# Revit family: IS_LDV_E2639_BIM_GB
name_source: partatom
category: Plumbing Fixtures
units: mm (PartAtom-declared; Revit-internal decimal feet)

## family parameters
Cut with Voids When Loaded = No
Host = Face
Maintain Annotation Orientation = No
OmniClass Number = 23.45.05.14.14.14
OmniClass Title = Clinic Sinks
Part Type = Normal
Room Calculation Point = No
Round Connector Dimension = Use Diameter
Shared = Yes

## types (1)
- E263901 - LDV BTW HF BIDET WHITE BXD
    Accessories = https://www.idealstandard.co.uk
    AreaUnits = millimeters
    Assembly Code = C1030200
    AssetType = Fixed
    BIMObjectName = IS_LDV_Bidet_E2639
    BarCode = 5017830562481
    Brand = Ideal Standard
    CWFU = 0
    Color = White
    ConnectionType = Plumbing
    Cost = 0 $
    Default Elevation = 400 mm  [stored 1.31234 ft]
    Description = La Dolce Vita® back-to-wall bidet, hidden wallfixation TT0293851, 1 taphole, with round overflow, white
    DrainSize = 46 mm  [stored 0.150919 ft]
    DurationUnit = year
    ECA = No
    EPD = https://www.idealstandard.co.uk
    ExpectedLife = 30
    Features = La Dolce Vita® back-to-wall bidet, hidden wallfixation TT0293851, 1 taphole, with round overflow, white, carton box, EU pallet
    Finish = white
    HWFU = 0
    Help = https://www.idealstandard.co.uk
    IfcExportAs = IfcSanitaryType
    IfcExportType = BIDET
    InstallationInstructions = https://www.idealstandard.co.uk
    LinearUnits = millimeters
    Manufacturer = Ideal Standard
    ManufacturerURL = https://www.idealstandard.co.uk
    Material = Fine Fireclay
    Model = E263901
    ModelNumber = E263901
    ModelReference = La Dolce Vita® back-to-wall bidet, hidden wallfixation TT0293851, 1 taphole, with round overflow, white
    NBSDescription = Bidets
    NBSReference = Pr_40_20_96_81
    Name = Bidet_LDV_E2639_IdealStandard
    NettWeight = 21
    NominalDepth = 563 mm
    NominalHeight = 400 mm  [stored 1.31234 ft]
    NominalLength = 563 mm
    NominalWidth = 360 mm
    ProductInformation = https://www.idealstandard.co.uk
    Shape = Sculptured
    Size = 360 x 563 x 400 mm
    Space = Internal
    URL = https://www.idealstandard.co.uk
    Uniclass2015Code = Pr_40_20_96_81
    Uniclass2015Description = Bidets
    Uniclass2015Title = Bidets
    Uniclass2015Version = Products v1.33
    Version = 1
    VolumeUnits = Litres
    WFU = 0
    WRAS = No
    WarrantyDescription = Manufacturers Warranty
    WarrantyDurationParts = 99
    WarrantyDurationUnit = year
    WarrantyGuarantorParts = Ideal Standard
    WaterEfficientProduct = No

note: [stored X ft] marks values corroborated as IEEE doubles in the binary element streams (Revit-internal decimal feet)

## geometry (parser evidence)
native form markers: Sweep x3
no freeform markers — native parametric forms only
